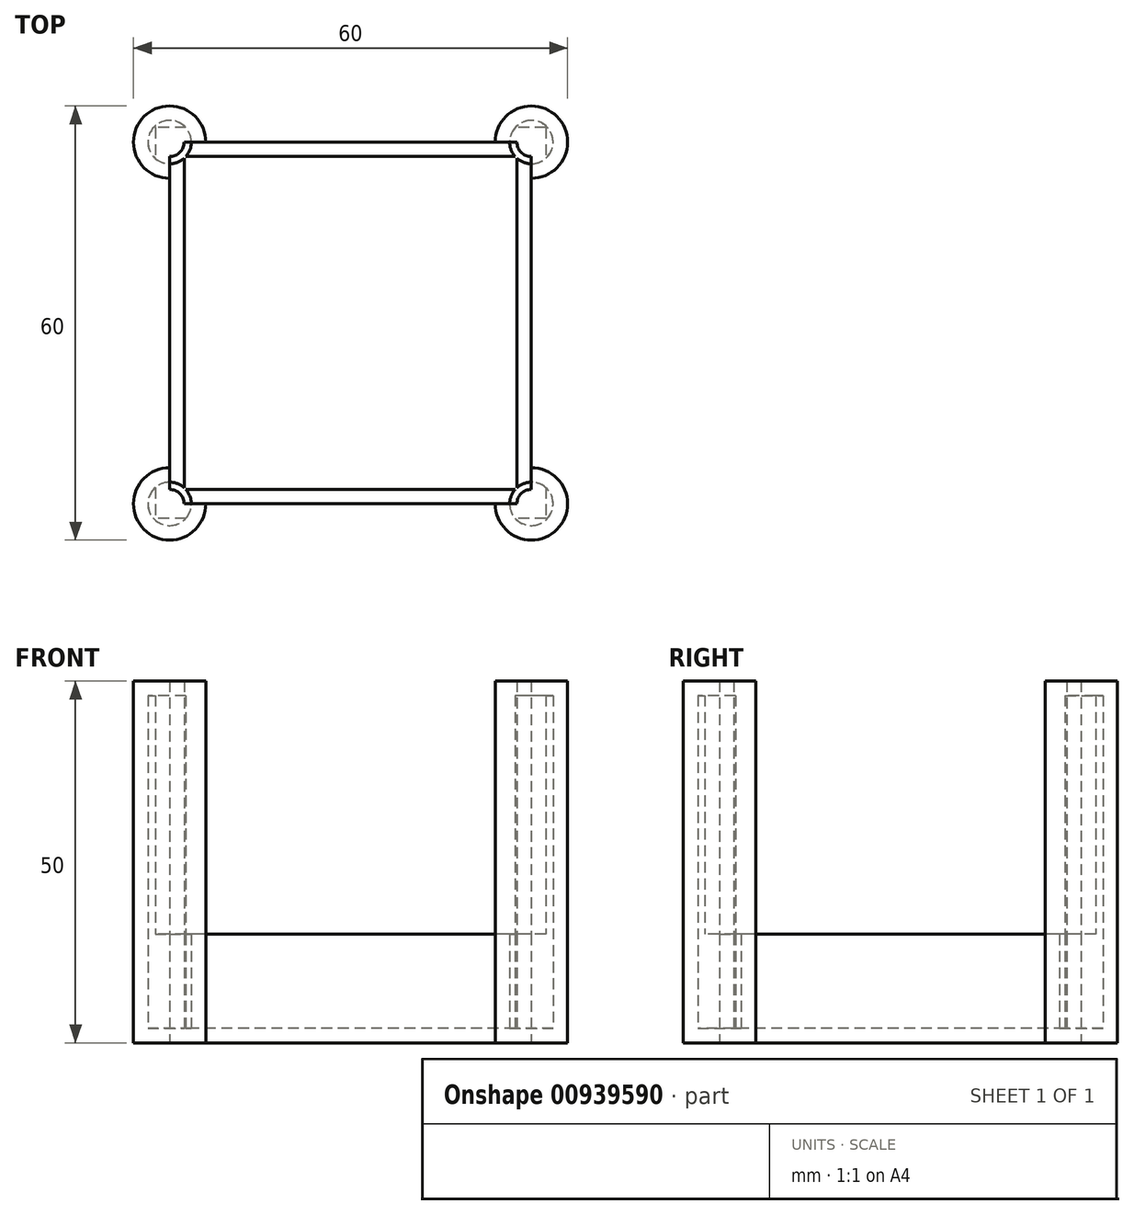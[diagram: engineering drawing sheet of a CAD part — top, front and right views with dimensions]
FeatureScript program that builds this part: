
annotation { "Feature Type Name" : "Feature", "Feature Type Description" : "" }
export const myFeature = defineFeature(function(context is Context, id is Id, definition is map)
    precondition{}
    {
        {
            var Q0;
            Q0=qCreatedBy(makeId("Top.planeOp"),FACE);
            var sketch = newSketch(context, id + "F0", { "sketchPlane" : qUnion([Q0])});
            skLineSegment(sketch, "E0.bottom", {"start": v(23, 25) * mm, "end": v(-23, 25) * mm});
            skLineSegment(sketch, "E0.top", {"start": v(23, -25) * mm, "end": v(-23, -25) * mm});
            skLineSegment(sketch, "E0.left", {"start": v(25, 23) * mm, "end": v(25, -23) * mm});
            skLineSegment(sketch, "E0.right", {"start": v(-25, 23) * mm, "end": v(-25, -23) * mm});
            skPoint(sketch, "E0.middle", {"position": v(0, 0) * mm});
            skArc(sketch, "E1", {"start": v(23, 25) * mm, "mid": v(23.59, 23.59) * mm, "end": v(25, 23) * mm});
            skArc(sketch, "E2", {"start": v(-25, 23) * mm, "mid": v(-23.59, 23.59) * mm, "end": v(-23, 25) * mm});
            skArc(sketch, "E3", {"start": v(-23, -25) * mm, "mid": v(-23.59, -23.59) * mm, "end": v(-25, -23) * mm});
            skArc(sketch, "E4", {"start": v(25, -23) * mm, "mid": v(23.59, -23.59) * mm, "end": v(23, -25) * mm});
            skArc(sketch, "E5", {"start": v(25, 20) * mm, "mid": v(28.54, 28.54) * mm, "end": v(20, 25) * mm});
            skArc(sketch, "E6", {"start": v(20, -25) * mm, "mid": v(28.54, -28.54) * mm, "end": v(25, -20) * mm});
            skArc(sketch, "E7", {"start": v(-25, -20) * mm, "mid": v(-28.54, -28.54) * mm, "end": v(-20, -25) * mm});
            skArc(sketch, "E8", {"start": v(-20, 25) * mm, "mid": v(-28.54, 28.54) * mm, "end": v(-25, 20) * mm});
            skSolve(sketch);
        }
        {
            var Q0;
            {var subQ7=sQuery(id+"F0.wireOp",EDGE,"E0.bottom");Q0=makeQuery(id+"F0.imprint","IMPRINT",FACE,{"disambiguationData":[TD([[makeQuery(id+"F0.imprint","IMPRINT",EDGE,{"derivedFrom":subQ7}),1.0]])]});}
            extrude(context, id + "F1", {"entities" : qUnion([Q0]), "depth" : 5 * mm, "offsetDistance" : 25 * mm});
        }
        {
            var Q0;
            {var subQ0=sQuery(id+"F0.wireOp",EDGE,"E4");var subQ1=makeQuery(id+"F0.imprint","INTERSECT",VERTEX,{"derivedFrom":[sQuery(id+"F0.wireOp",EDGE,"E0.left"),subQ0]});Q0=makeQuery(id+"F0.imprint","IMPRINT",FACE,{"disambiguationData":[TD([[makeQuery(id+"F0.imprint","IMPRINT",EDGE,{"disambiguationData":[TD([[subQ1,-1.0]])],"derivedFrom":subQ0}),1.0]])]});}
            var Q1;
            {var subQ0=sQuery(id+"F0.wireOp",EDGE,"E3");var subQ1=makeQuery(id+"F0.imprint","INTERSECT",VERTEX,{"derivedFrom":[sQuery(id+"F0.wireOp",EDGE,"E0.top"),subQ0]});Q1=makeQuery(id+"F0.imprint","IMPRINT",FACE,{"disambiguationData":[TD([[makeQuery(id+"F0.imprint","IMPRINT",EDGE,{"disambiguationData":[TD([[subQ1,-1.0]])],"derivedFrom":subQ0}),1.0]])]});}
            var Q2;
            {var subQ0=sQuery(id+"F0.wireOp",EDGE,"E1");var subQ1=makeQuery(id+"F0.imprint","INTERSECT",VERTEX,{"derivedFrom":[sQuery(id+"F0.wireOp",EDGE,"E0.bottom"),subQ0]});Q2=makeQuery(id+"F0.imprint","IMPRINT",FACE,{"disambiguationData":[TD([[makeQuery(id+"F0.imprint","IMPRINT",EDGE,{"disambiguationData":[TD([[subQ1,-1.0]])],"derivedFrom":subQ0}),1.0]])]});}
            var Q3;
            {var subQ0=sQuery(id+"F0.wireOp",EDGE,"E2");var subQ1=makeQuery(id+"F0.imprint","INTERSECT",VERTEX,{"derivedFrom":[sQuery(id+"F0.wireOp",EDGE,"E0.bottom"),subQ0]});Q3=makeQuery(id+"F0.imprint","IMPRINT",FACE,{"disambiguationData":[TD([[makeQuery(id+"F0.imprint","IMPRINT",EDGE,{"disambiguationData":[TD([[subQ1,-1.0]])],"derivedFrom":subQ0}),1.0]])]});}
            extrude(context, id + "F2", {"entities" : qUnion([Q0, Q1, Q2, Q3]), "operationType" : NewBodyOperationType.ADD, "depth" : 50 * mm, "offsetDistance" : 25 * mm});
        }
        {
            var Q0;
            Q0=makeQuery(id+"F1.opExtrude","CAP_FACE",FACE,{"disambiguationData":[OSD([sQuery(id+"F0.wireOp",EDGE,"E0.bottom"),sQuery(id+"F0.wireOp",EDGE,"E0.top"),sQuery(id+"F0.wireOp",EDGE,"E0.left"),sQuery(id+"F0.wireOp",EDGE,"E0.right"),sQuery(id+"F0.wireOp",EDGE,"E1"),sQuery(id+"F0.wireOp",EDGE,"E2"),sQuery(id+"F0.wireOp",EDGE,"E3"),sQuery(id+"F0.wireOp",EDGE,"E4")])],"isStart":false});
            extrude(context, id + "F3", {"entities" : qUnion([Q0]), "operationType" : NewBodyOperationType.ADD, "depth" : 10 * mm, "offsetDistance" : 25 * mm});
        }
        {
            var Q0;
            Q0=makeQuery(id+"F3.opExtrude","CAP_FACE",FACE,{"disambiguationData":[OSD([sQuery(id+"F0.wireOp",EDGE,"E0.bottom"),sQuery(id+"F0.wireOp",EDGE,"E0.top"),sQuery(id+"F0.wireOp",EDGE,"E0.left"),sQuery(id+"F0.wireOp",EDGE,"E0.right"),sQuery(id+"F0.wireOp",EDGE,"E1"),sQuery(id+"F0.wireOp",EDGE,"E2"),sQuery(id+"F0.wireOp",EDGE,"E3"),sQuery(id+"F0.wireOp",EDGE,"E4")])],"isStart":false});
            shell(context, id + "F4", {"entities" : qUnion([Q0]), "thickness" : 2 * mm});
        }
    });
